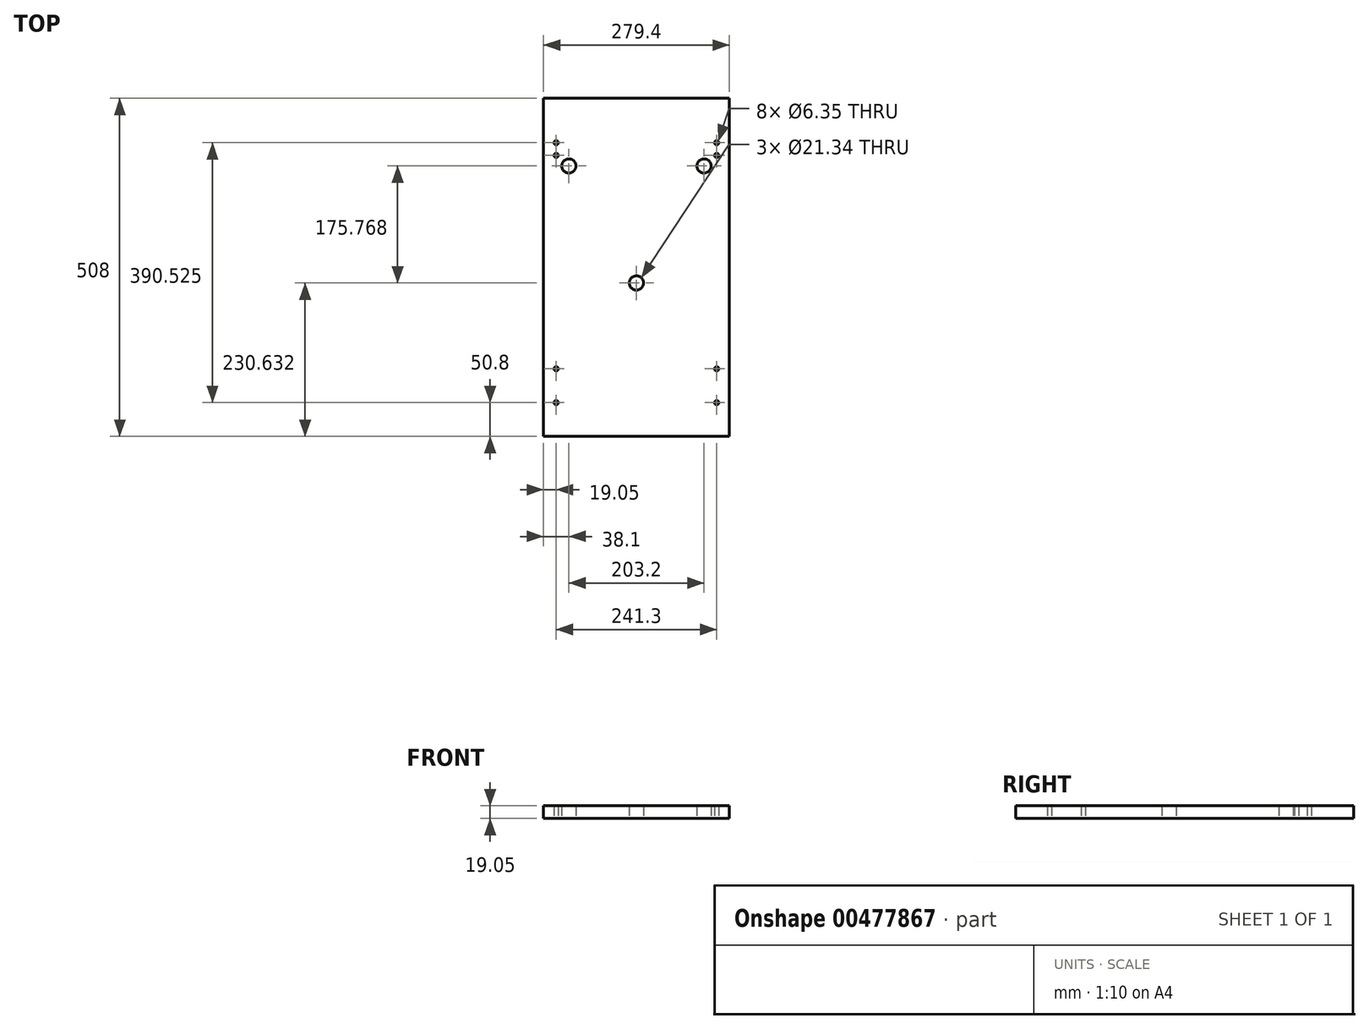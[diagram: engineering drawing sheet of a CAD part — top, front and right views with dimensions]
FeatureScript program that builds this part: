
annotation { "Feature Type Name" : "Feature", "Feature Type Description" : "" }
export const myFeature = defineFeature(function(context is Context, id is Id, definition is map)
    precondition{}
    {
        {
            var Q0;
            Q0=qCreatedBy(makeId("Top.planeOp"),FACE);
            var sketch = newSketch(context, id + "F0", { "sketchPlane" : qUnion([Q0])});
            skLineSegment(sketch, "E0", {"start": v(0, 0) * mm, "end": v(0, 508) * mm});
            skLineSegment(sketch, "E1", {"start": v(0, 508) * mm, "end": v(279.4, 508) * mm});
            skLineSegment(sketch, "E2", {"start": v(279.4, 508) * mm, "end": v(279.4, 0) * mm});
            skLineSegment(sketch, "E3", {"start": v(279.4, 0) * mm, "end": v(0, 0) * mm});
            skLineSegment(sketch, "E4.bottom", {"start": v(19.05, 101.6) * mm, "end": v(260.35, 101.6) * mm, "construction": true});
            skLineSegment(sketch, "E4.top", {"start": v(19.05, 50.8) * mm, "end": v(260.35, 50.8) * mm, "construction": true});
            skLineSegment(sketch, "E4.left", {"start": v(19.05, 101.6) * mm, "end": v(19.05, 50.8) * mm, "construction": true});
            skLineSegment(sketch, "E4.right", {"start": v(260.35, 101.6) * mm, "end": v(260.35, 50.8) * mm, "construction": true});
            skPoint(sketch, "E5", {"position": v(19.05, 101.6) * mm});
            skPoint(sketch, "E6", {"position": v(260.35, 50.8) * mm});
            skPoint(sketch, "E7", {"position": v(19.05, 50.8) * mm});
            skLineSegment(sketch, "E8", {"start": v(19.05, 101.6) * mm, "end": v(0, 101.6) * mm, "construction": true});
            skLineSegment(sketch, "E9", {"start": v(260.35, 50.8) * mm, "end": v(279.4, 50.8) * mm, "construction": true});
            skLineSegment(sketch, "E10", {"start": v(19.05, 441.32) * mm, "end": v(260.35, 441.32) * mm, "construction": true});
            skLineSegment(sketch, "E11", {"start": v(260.35, 422.27) * mm, "end": v(19.05, 422.27) * mm, "construction": true});
            skLineSegment(sketch, "E12", {"start": v(19.05, 441.32) * mm, "end": v(19.05, 422.27) * mm, "construction": true});
            skLineSegment(sketch, "E13", {"start": v(260.35, 441.33) * mm, "end": v(260.35, 422.27) * mm, "construction": true});
            skLineSegment(sketch, "E14", {"start": v(19.05, 441.32) * mm, "end": v(0, 441.32) * mm, "construction": true});
            skLineSegment(sketch, "E15", {"start": v(260.35, 422.27) * mm, "end": v(279.4, 422.27) * mm, "construction": true});
            skLineSegment(sketch, "E16", {"start": v(19.05, 76.2) * mm, "end": v(0, 76.2) * mm, "construction": true});
            skLineSegment(sketch, "E17", {"start": v(260.35, 76.2) * mm, "end": v(279.4, 76.2) * mm, "construction": true});
            skLineSegment(sketch, "E18", {"start": v(260.35, 431.8) * mm, "end": v(279.4, 431.8) * mm, "construction": true});
            skLineSegment(sketch, "E19", {"start": v(0, 406.4) * mm, "end": v(38.1, 406.4) * mm, "construction": true});
            skLineSegment(sketch, "E20", {"start": v(38.1, 406.4) * mm, "end": v(241.3, 406.4) * mm, "construction": true});
            skLineSegment(sketch, "E21", {"start": v(241.3, 406.4) * mm, "end": v(279.4, 406.4) * mm, "construction": true});
            skLineSegment(sketch, "E22", {"start": v(139.7, 406.4) * mm, "end": v(139.7, 230.63) * mm, "construction": true});
            skPoint(sketch, "E23", {"position": v(38.1, 406.4) * mm});
            skPoint(sketch, "E24", {"position": v(241.3, 406.4) * mm});
            skPoint(sketch, "E25", {"position": v(139.7, 230.63) * mm});
            skSolve(sketch);
        }
        {
            var Q0;
            Q0=makeQuery(id+"F0.imprint","IMPRINT",FACE,{"disambiguationData":[TD([[makeQuery(id+"F0.imprint","IMPRINT",EDGE,{"derivedFrom":sQuery(id+"F0.wireOp",EDGE,"E0")}),-1.0]])]});
            extrude(context, id + "F1", {"entities" : qUnion([Q0]), "depth" : 19.05 * mm});
        }
        {
            var Q0;
            Q0=sQuery(id+"F0.wireOp",VERTEX,"E5");
            var Q1;
            Q1=sQuery(id+"F0.wireOp",VERTEX,"E4.right.start");
            var Q2;
            Q2=sQuery(id+"F0.wireOp",VERTEX,"E6");
            var Q3;
            Q3=sQuery(id+"F0.wireOp",VERTEX,"E7");
            var Q4;
            Q4=makeQuery(id+"F1.opExtrude","SWEPT_BODY",BODY,{"disambiguationData":[OSD([sQuery(id+"F0.wireOp",EDGE,"E0"),sQuery(id+"F0.wireOp",EDGE,"E1"),sQuery(id+"F0.wireOp",EDGE,"E2"),sQuery(id+"F0.wireOp",EDGE,"E3")])]});
            hole(context, id + "F2", {"style" : HoleStyle.SIMPLE, "endStyle" : HoleEndStyle.THROUGH, "oppositeDirection" : true, "holeDiameter" : 6.35 * mm, "isTappedThrough" : true, "tappedDepth" : 12.7 * mm, "tapClearance" : 3, "locations" : qUnion([Q0, Q1, Q2, Q3]), "scope" : qUnion([Q4])});
        }
        {
            var Q0;
            Q0=sQuery(id+"F0.wireOp",VERTEX,"E10.start");
            var Q1;
            Q1=sQuery(id+"F0.wireOp",VERTEX,"E11.end");
            var Q2;
            Q2=sQuery(id+"F0.wireOp",VERTEX,"E13.end");
            var Q3;
            Q3=sQuery(id+"F0.wireOp",VERTEX,"E13.start");
            var Q4;
            Q4=makeQuery(id+"F1.opExtrude","SWEPT_BODY",BODY,{"disambiguationData":[OSD([sQuery(id+"F0.wireOp",EDGE,"E0"),sQuery(id+"F0.wireOp",EDGE,"E1"),sQuery(id+"F0.wireOp",EDGE,"E2"),sQuery(id+"F0.wireOp",EDGE,"E3")])]});
            hole(context, id + "F3", {"style" : HoleStyle.SIMPLE, "endStyle" : HoleEndStyle.THROUGH, "oppositeDirection" : true, "holeDiameter" : 6.35 * mm, "isTappedThrough" : true, "tappedDepth" : 12.7 * mm, "tapClearance" : 3, "locations" : qUnion([Q0, Q1, Q2, Q3]), "scope" : qUnion([Q4])});
        }
        {
            var Q0;
            Q0=sQuery(id+"F0.wireOp",VERTEX,"E23");
            var Q1;
            Q1=sQuery(id+"F0.wireOp",VERTEX,"E24");
            var Q2;
            Q2=sQuery(id+"F0.wireOp",VERTEX,"E25");
            var Q3;
            Q3=makeQuery(id+"F1.opExtrude","SWEPT_BODY",BODY,{"disambiguationData":[OSD([sQuery(id+"F0.wireOp",EDGE,"E0"),sQuery(id+"F0.wireOp",EDGE,"E1"),sQuery(id+"F0.wireOp",EDGE,"E2"),sQuery(id+"F0.wireOp",EDGE,"E3")])]});
            hole(context, id + "F4", {"style" : HoleStyle.SIMPLE, "endStyle" : HoleEndStyle.THROUGH, "oppositeDirection" : true, "holeDiameter" : 21.34 * mm, "isTappedThrough" : true, "tappedDepth" : 12.7 * mm, "tapClearance" : 3, "locations" : qUnion([Q0, Q1, Q2]), "scope" : qUnion([Q3])});
        }
    });
